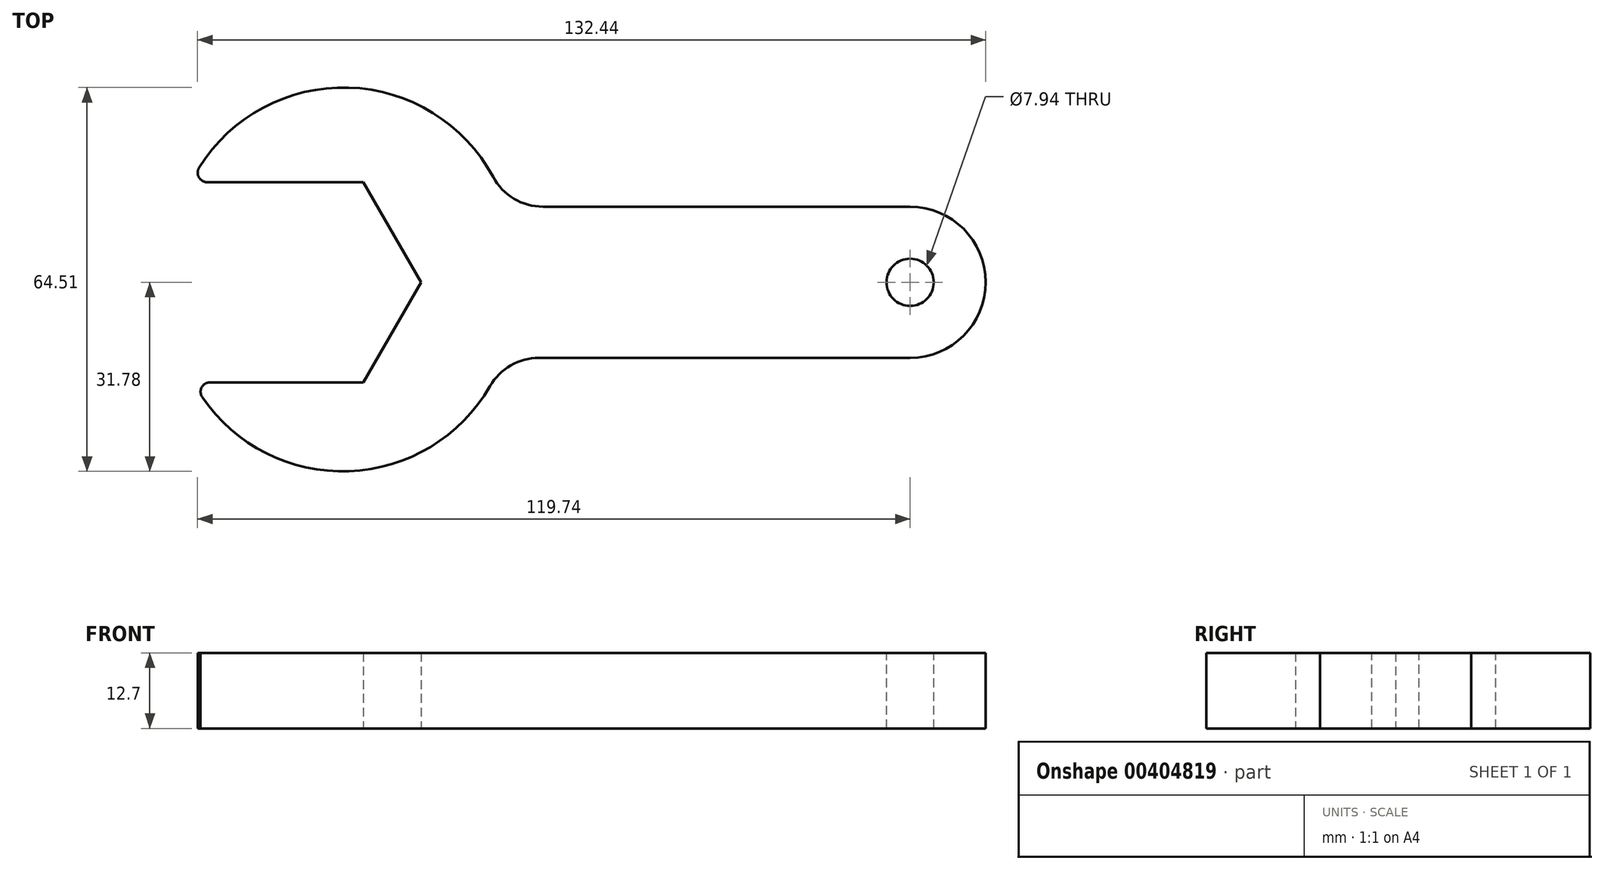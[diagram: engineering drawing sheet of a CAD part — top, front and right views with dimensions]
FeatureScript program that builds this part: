
annotation { "Feature Type Name" : "Feature", "Feature Type Description" : "" }
export const myFeature = defineFeature(function(context is Context, id is Id, definition is map)
    precondition{}
    {
        {
            var Q0;
            Q0=qCreatedBy(makeId("Top.planeOp"),FACE);
            var sketch = newSketch(context, id + "F0", { "sketchPlane" : qUnion([Q0])});
            skCircle(sketch, "E0.cCircle", {"center": v(0, 0) * mm, "radius": 16.83 * mm, "construction": true});
            skLineSegment(sketch, "E0.0", {"start": v(-9.72, 16.83) * mm, "end": v(9.72, 16.83) * mm});
            skLineSegment(sketch, "E0.1", {"start": v(9.72, 16.83) * mm, "end": v(19.43, 0) * mm});
            skLineSegment(sketch, "E0.2", {"start": v(19.43, 0) * mm, "end": v(9.72, -16.83) * mm});
            skLineSegment(sketch, "E0.3", {"start": v(9.72, -16.83) * mm, "end": v(-9.72, -16.83) * mm});
            skLineSegment(sketch, "E0.4", {"start": v(-9.72, -16.83) * mm, "end": v(-19.43, 0) * mm});
            skLineSegment(sketch, "E0.5", {"start": v(-19.43, 0) * mm, "end": v(-9.72, 16.83) * mm});
            skPoint(sketch, "E0.0.midPoint", {"position": v(0, 16.83) * mm});
            skLineSegment(sketch, "E1", {"start": v(-9.72, 16.83) * mm, "end": v(-19.25, 16.83) * mm});
            skLineSegment(sketch, "E2", {"start": v(-9.72, -16.83) * mm, "end": v(-18.88, -16.83) * mm});
            skCircle(sketch, "E3", {"center": v(101.6, 0) * mm, "radius": 12.7 * mm});
            skLineSegment(sketch, "E4", {"start": v(101.6, 12.7) * mm, "end": v(33.63, 12.7) * mm});
            skLineSegment(sketch, "E5", {"start": v(101.6, -12.7) * mm, "end": v(33.19, -12.7) * mm});
            skArc(sketch, "E6", {"start": v(-18.88, -16.83) * mm, "mid": v(8.5, -31.69) * mm, "end": v(33.19, -12.7) * mm});
            skArc(sketch, "E7.trimOffspring", {"start": v(33.63, 12.7) * mm, "mid": v(8.59, 32.65) * mm, "end": v(-19.25, 16.83) * mm});
            skPoint(sketch, "E8.center.orphan", {"position": v(6.24, 3.19) * mm});
            skSolve(sketch);
        }
        {
            var Q0;
            Q0=makeQuery(id+"F0.imprint","IMPRINT",FACE,{"disambiguationData":[TD([[makeQuery(id+"F0.imprint","IMPRINT",EDGE,{"derivedFrom":sQuery(id+"F0.wireOp",EDGE,"E0.0")}),1.0]])]});
            var Q1;
            {var subQ0=sQuery(id+"F0.wireOp",EDGE,"E3");var subQ1=makeQuery(id+"F0.imprint","INTERSECT",VERTEX,{"derivedFrom":[subQ0,sQuery(id+"F0.wireOp",EDGE,"E4")]});Q1=makeQuery(id+"F0.imprint","IMPRINT",FACE,{"disambiguationData":[TD([[makeQuery(id+"F0.imprint","IMPRINT",EDGE,{"disambiguationData":[TD([[subQ1,-1.0]])],"derivedFrom":subQ0}),1.0]])]});}
            var Q2;
            {var subQ1=sQuery(id+"F0.wireOp",EDGE,"E4");Q2=makeQuery(id+"F0.imprint","IMPRINT",FACE,{"disambiguationData":[TD([[makeQuery(id+"F0.imprint","IMPRINT",EDGE,{"derivedFrom":subQ1}),1.0]])]});}
            extrude(context, id + "F1", {"entities" : qUnion([Q0, Q1, Q2]), "depth" : 12.7 * mm});
        }
        {
            var Q0;
            Q0=makeQuery(id+"F1.opExtrude","CAP_FACE",FACE,{"disambiguationData":[OSD([sQuery(id+"F0.wireOp",EDGE,"E0.0"),sQuery(id+"F0.wireOp",EDGE,"E0.1"),sQuery(id+"F0.wireOp",EDGE,"E0.2"),sQuery(id+"F0.wireOp",EDGE,"E0.3"),sQuery(id+"F0.wireOp",EDGE,"E1"),sQuery(id+"F0.wireOp",EDGE,"E2"),sQuery(id+"F0.wireOp",EDGE,"E3"),sQuery(id+"F0.wireOp",EDGE,"E4"),sQuery(id+"F0.wireOp",EDGE,"E5"),sQuery(id+"F0.wireOp",EDGE,"e8fc7d6f-e446-4141-8ea7-832e3ede0361.filletArc"),sQuery(id+"F0.wireOp",EDGE,"82861d57-7e7a-439f-97a6-c388854d8430.filletArc"),sQuery(id+"F0.wireOp",EDGE,"E6"),sQuery(id+"F0.wireOp",EDGE,"E7.trimOffspring")])],"isStart":false});
            var sketch = newSketch(context, id + "F2", { "sketchPlane" : qUnion([Q0])});
            skCircle(sketch, "E9", {"center": v(101.6, 0) * mm, "radius": 3.97 * mm});
            skSolve(sketch);
        }
        {
            var Q0;
            Q0 = qSketchRegion(id + "F2", true);
            extrude(context, id + "F3", {"entities" : qUnion([Q0]), "operationType" : NewBodyOperationType.REMOVE, "endBound" : BoundingType.THROUGH_ALL, "oppositeDirection" : true, "depth" : 25.4 * mm});
        }
        {
            var Q0;
            Q0=makeQuery(id+"F1.opExtrude","SWEPT_EDGE",EDGE,{"disambiguationData":[OSD([sQuery(id+"F0.wireOp",EDGE,"E4"),sQuery(id+"F0.wireOp",EDGE,"E7.trimOffspring")])]});
            var Q1;
            Q1=makeQuery(id+"F1.opExtrude","SWEPT_EDGE",EDGE,{"disambiguationData":[OSD([sQuery(id+"F0.wireOp",EDGE,"E5"),sQuery(id+"F0.wireOp",EDGE,"E6")])]});
            fillet(context, id + "F4", {"entities" : qUnion([Q0, Q1]), "radius" : 9.52 * mm, "tangentPropagation" : true, "allowEdgeOverflow" : false});
        }
        {
            var Q0;
            Q0=makeQuery(id+"F1.opExtrude","SWEPT_EDGE",EDGE,{"disambiguationData":[OSD([sQuery(id+"F0.wireOp",EDGE,"E1"),sQuery(id+"F0.wireOp",EDGE,"E7.trimOffspring")])]});
            var Q1;
            Q1=makeQuery(id+"F1.opExtrude","SWEPT_EDGE",EDGE,{"disambiguationData":[OSD([sQuery(id+"F0.wireOp",EDGE,"E2"),sQuery(id+"F0.wireOp",EDGE,"E6")])]});
            fillet(context, id + "F5", {"entities" : qUnion([Q0, Q1]), "radius" : 1.59 * mm, "tangentPropagation" : true, "allowEdgeOverflow" : false});
        }
    });
